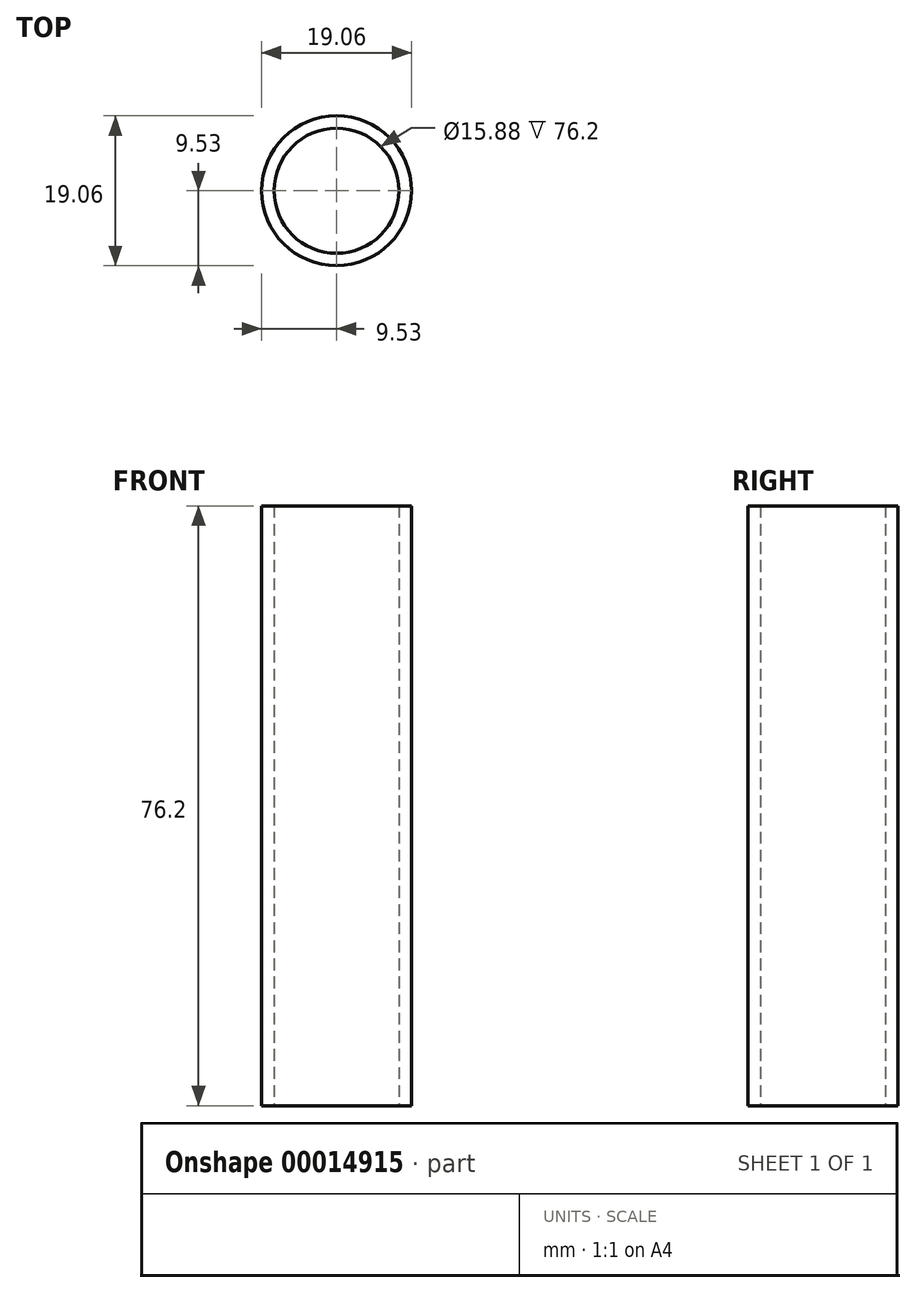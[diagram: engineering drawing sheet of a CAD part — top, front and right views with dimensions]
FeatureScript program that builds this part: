
annotation { "Feature Type Name" : "Feature", "Feature Type Description" : "" }
export const myFeature = defineFeature(function(context is Context, id is Id, definition is map)
    precondition{}
    {
        {
            var Q0;
            Q0=qCreatedBy(makeId("Top.planeOp"),FACE);
            var sketch = newSketch(context, id + "F0", { "sketchPlane" : qUnion([Q0])});
            skCircle(sketch, "E0", {"center": v(0, 0) * mm, "radius": 7.94 * mm});
            skCircle(sketch, "E1", {"center": v(0, 0) * mm, "radius": 9.53 * mm});
            skSolve(sketch);
        }
        {
            var Q0;
            Q0=makeQuery(id+"F0.imprint","IMPRINT",FACE,{"disambiguationData":[TD([[makeQuery(id+"F0.imprint","IMPRINT",EDGE,{"derivedFrom":sQuery(id+"F0.wireOp",EDGE,"E0")}),-1.0]])]});
            extrude(context, id + "F1", {"entities" : qUnion([Q0]), "depth" : 76.2 * mm});
        }
    });
